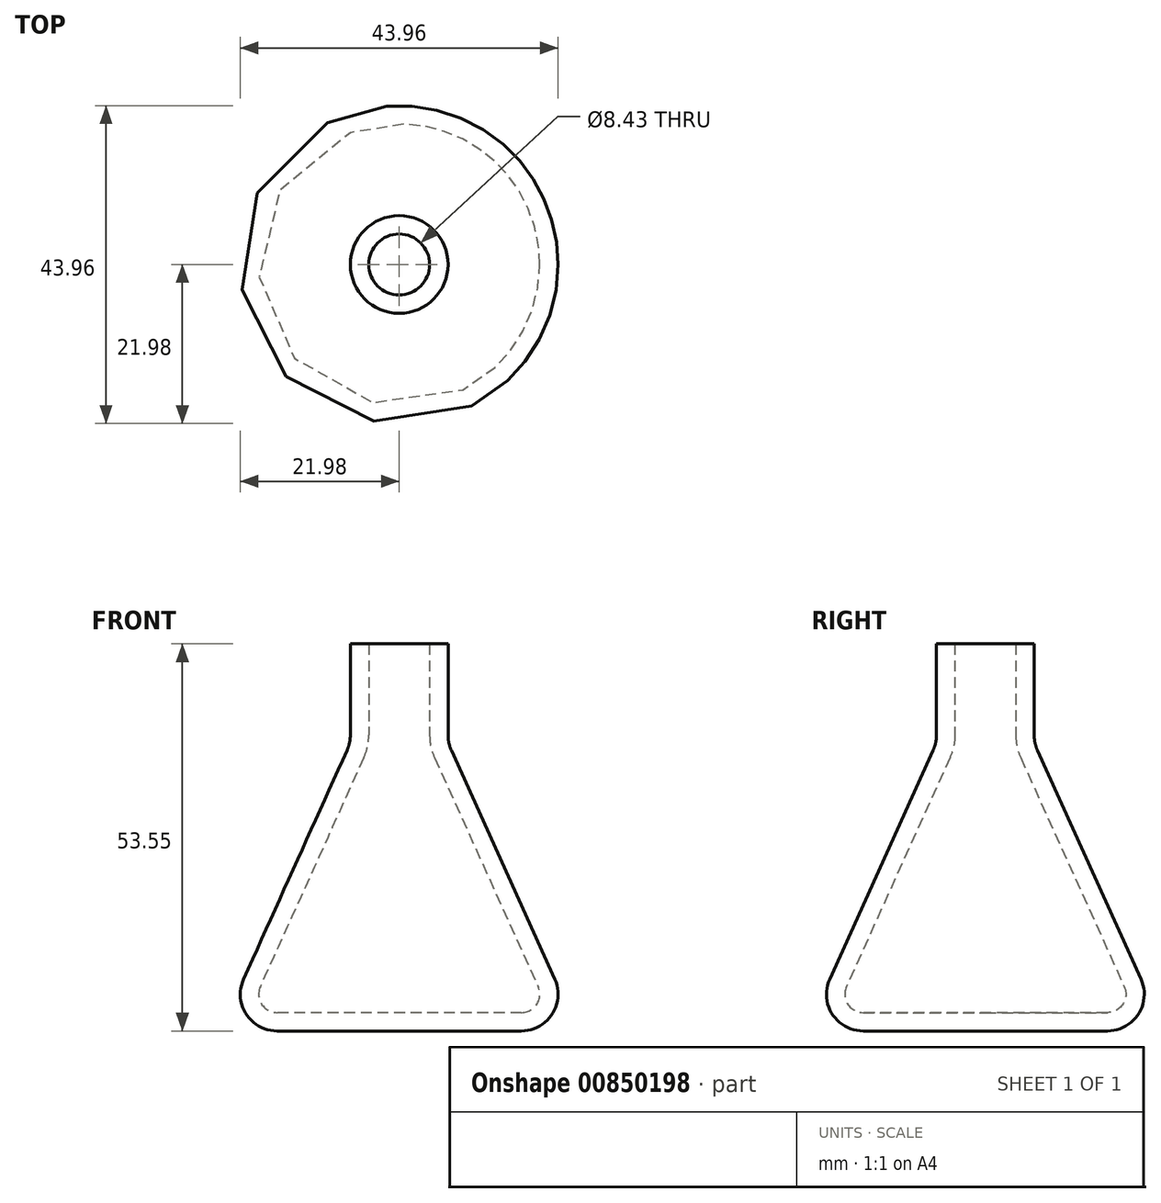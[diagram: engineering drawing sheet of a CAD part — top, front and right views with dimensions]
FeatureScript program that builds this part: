
annotation { "Feature Type Name" : "Feature", "Feature Type Description" : "" }
export const myFeature = defineFeature(function(context is Context, id is Id, definition is map)
    precondition{}
    {
        {
            var Q0;
            Q0=qCreatedBy(makeId("Front.planeOp"),FACE);
            var sketch = newSketch(context, id + "F0", { "sketchPlane" : qUnion([Q0])});
            skLineSegment(sketch, "E0", {"start": v(-24.77, 0) * mm, "end": v(0, 0) * mm});
            skLineSegment(sketch, "E1", {"start": v(-24.77, 0) * mm, "end": v(-6.75, 39.84) * mm});
            skLineSegment(sketch, "E2", {"start": v(-6.75, 39.84) * mm, "end": v(-6.75, 53.55) * mm});
            skLineSegment(sketch, "E3", {"start": v(-6.75, 53.55) * mm, "end": v(0, 53.55) * mm});
            skLineSegment(sketch, "E4", {"start": v(0, 0) * mm, "end": v(0, 53.55) * mm});
            skSolve(sketch);
        }
        {
            var Q0;
            Q0 = qSketchRegion(id + "F0", true);
            var Q1;
            Q1=sQuery(id+"F0.wireOp",EDGE,"E4");
            revolve(context, id + "F1", {"surfaceOperationType" : NewSurfaceOperationType.NEW, "entities" : qUnion([Q0]), "axis" : qUnion([Q1]), "revolveType" : RevolveType.FULL});
        }
        {
            var Q0;
            Q0=makeQuery(id+"F1.opRevolve","SWEPT_FACE",FACE,{"disambiguationData":[OSD([sQuery(id+"F0.wireOp",EDGE,"E1")])]});
            fillet(context, id + "F2", {"entities" : qUnion([Q0]), "radius" : 5.08 * mm, "tangentPropagation" : true, "allowEdgeOverflow" : false});
        }
        {
            var Q0;
            Q0=makeQuery(id+"F1.opRevolve","SWEPT_FACE",FACE,{"disambiguationData":[OSD([sQuery(id+"F0.wireOp",EDGE,"E3")])]});
            shell(context, id + "F3", {"entities" : qUnion([Q0]), "thickness" : 2.54 * mm});
        }
    });
